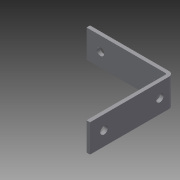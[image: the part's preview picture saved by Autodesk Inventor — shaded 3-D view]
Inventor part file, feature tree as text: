
AUTODESK INVENTOR PART (.ipt)
format: ipt  version: 2013 (Build 170138000, 138)  size: 141,312 bytes
history: native  units: in
note: dims shown in document units (in); Inventor stores cm internally (conversion verified against a paired STEP export)
features: sheet_metal_op x4, other x4, sketch x3
ambient origin geometry x8: Origin, YZ Plane, XZ Plane, XY Plane, X Axis, Y Axis, Z Axis, Center Point
bodies: Solid1 (feature_tree)
feature tree (11):
  sheet_metal_op  "Face1"
  sheet_metal_op  "Flange1"
  sketch  "Sketch1"  dims[d0=1.0in]
  other  "Plate1"
  sketch  "Sketch2"  dims[d1=3.0in]
  other  "Plate2"
  sheet_metal_op  "Bend1"
  sheet_metal_op  "Corner1"
  sketch  "Sketch3"  dims[d2=0.266in d3=0.266in d4=0.5in d5=0.5in d6=0.5in d7=0.5in d8=0.125in d9=0.125in d10=0.0625in d11=0.25in d12=0.125in d13=3.0in d14=90.0deg d15=0.05in d16=0.5in d17=0.125in d18=0.125in d19=0.266in d20=0.266in d22=0.5in d23=0.5in d24=0.5in d25=0.125in d26=0.0in d27=2.0in]
  other  "Cut1"
  other  "Definition1"
